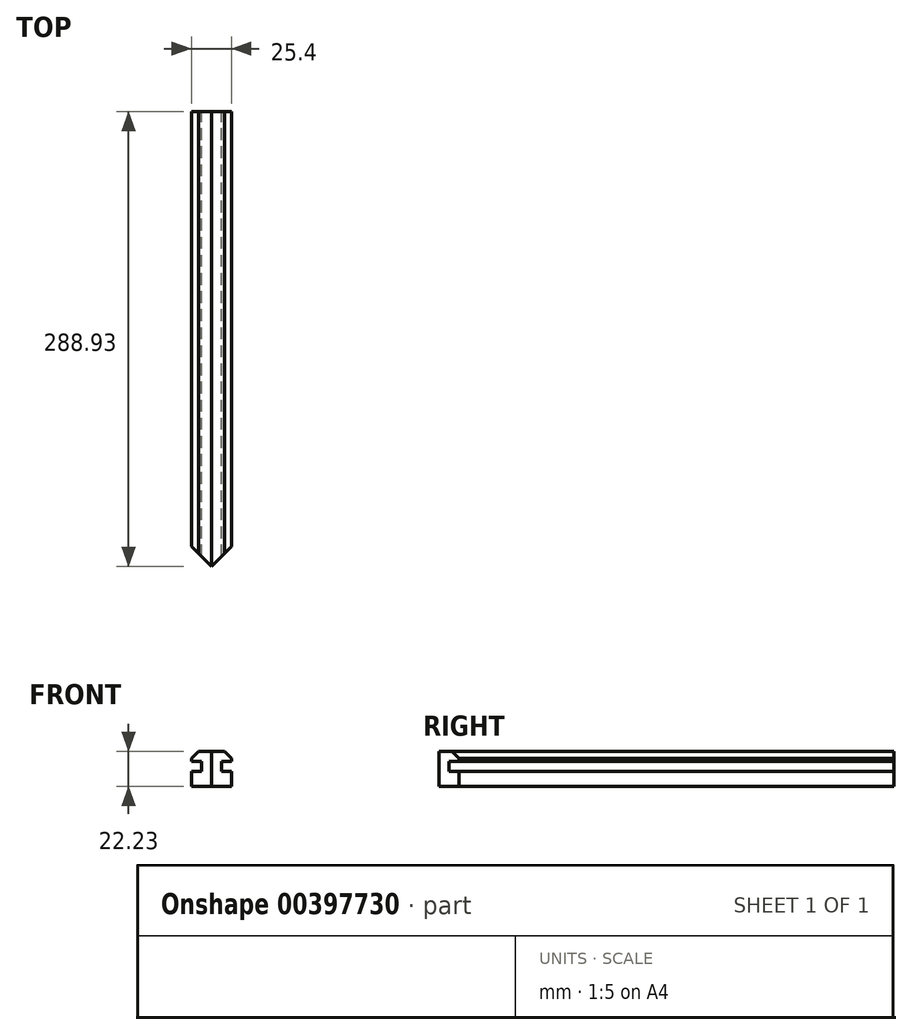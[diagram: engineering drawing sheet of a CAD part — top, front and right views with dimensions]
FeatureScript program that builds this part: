
annotation { "Feature Type Name" : "Feature", "Feature Type Description" : "" }
export const myFeature = defineFeature(function(context is Context, id is Id, definition is map)
    precondition{}
    {
        {
            var Q0;
            Q0=qCreatedBy(makeId("Front.planeOp"),FACE);
            var sketch = newSketch(context, id + "F0", { "sketchPlane" : qUnion([Q0])});
            skLineSegment(sketch, "E0.bottom", {"start": v(0, 0) * mm, "end": v(12.7, 0) * mm});
            skLineSegment(sketch, "E0.top", {"start": v(0, 22.23) * mm, "end": v(8.2, 22.22) * mm});
            skLineSegment(sketch, "E0.left", {"start": v(0, 0) * mm, "end": v(0, 22.23) * mm});
            skLineSegment(sketch, "E0.right", {"start": v(12.7, 0) * mm, "end": v(12.7, 9.52) * mm});
            skLineSegment(sketch, "E1.bottom", {"start": v(12.7, 15.88) * mm, "end": v(6.35, 15.88) * mm});
            skLineSegment(sketch, "E1.top", {"start": v(12.7, 9.52) * mm, "end": v(6.35, 9.52) * mm});
            skLineSegment(sketch, "E1.right", {"start": v(6.35, 15.88) * mm, "end": v(6.35, 9.52) * mm});
            skLineSegment(sketch, "E2.trimOffspring", {"start": v(12.7, 15.88) * mm, "end": v(12.7, 17.73) * mm});
            skLineSegment(sketch, "E3", {"start": v(12.7, 17.73) * mm, "end": v(8.2, 22.22) * mm});
            skSolve(sketch);
        }
        {
            var Q0;
            Q0=makeQuery(id+"F0.imprint","IMPRINT",FACE,{"disambiguationData":[TD([[makeQuery(id+"F0.imprint","IMPRINT",EDGE,{"derivedFrom":sQuery(id+"F0.wireOp",EDGE,"E0.bottom")}),1.0]])]});
            extrude(context, id + "F1", {"entities" : qUnion([Q0]), "depth" : 288.93 * mm});
        }
        {
            var Q0;
            Q0=makeQuery(id+"F1.opExtrude","SWEPT_FACE",FACE,{"disambiguationData":[OSD([sQuery(id+"F0.wireOp",EDGE,"E0.bottom")])]});
            var sketch = newSketch(context, id + "F2", { "sketchPlane" : qUnion([Q0])});
            skLineSegment(sketch, "E4", {"start": v(0, 288.93) * mm, "end": v(12.7, 276.23) * mm});
            skLineSegment(sketch, "E5", {"start": v(12.7, 276.23) * mm, "end": v(12.7, 288.93) * mm});
            skLineSegment(sketch, "E6", {"start": v(12.7, 288.93) * mm, "end": v(0, 288.93) * mm});
            skLineSegment(sketch, "E7", {"start": v(0, 0) * mm, "end": v(12.7, 12.7) * mm});
            skLineSegment(sketch, "E8", {"start": v(12.7, 12.7) * mm, "end": v(12.7, 0) * mm});
            skLineSegment(sketch, "E9", {"start": v(12.7, 0) * mm, "end": v(0, 0) * mm});
            skSolve(sketch);
        }
        {
            var Q0;
            Q0=makeQuery(id+"F2.imprint","IMPRINT",FACE,{"disambiguationData":[TD([[makeQuery(id+"F2.imprint","IMPRINT",EDGE,{"derivedFrom":sQuery(id+"F2.wireOp",EDGE,"E4")}),1.0]])]});
            extrude(context, id + "F3", {"entities" : qUnion([Q0]), "operationType" : NewBodyOperationType.REMOVE, "endBound" : BoundingType.THROUGH_ALL, "oppositeDirection" : true, "depth" : 25.4 * mm});
        }
        {
            var Q0;
            Q0=makeQuery(id+"F1.opExtrude","SWEPT_BODY",BODY,{"disambiguationData":[OSD([sQuery(id+"F0.wireOp",EDGE,"E0.bottom"),sQuery(id+"F0.wireOp",EDGE,"E0.top"),sQuery(id+"F0.wireOp",EDGE,"E0.left"),sQuery(id+"F0.wireOp",EDGE,"E0.right"),sQuery(id+"F0.wireOp",EDGE,"E1.bottom"),sQuery(id+"F0.wireOp",EDGE,"E1.top"),sQuery(id+"F0.wireOp",EDGE,"E1.right"),sQuery(id+"F0.wireOp",EDGE,"E2.trimOffspring"),sQuery(id+"F0.wireOp",EDGE,"E3")])]});
            var Q1;
            Q1=makeQuery(id+"F1.opExtrude","SWEPT_FACE",FACE,{"disambiguationData":[OSD([sQuery(id+"F0.wireOp",EDGE,"E0.left")])]});
            mirror(context, id + "F4", {"entities" : qUnion([Q0]), "mirrorPlane" : qUnion([Q1])});
        }
    });
